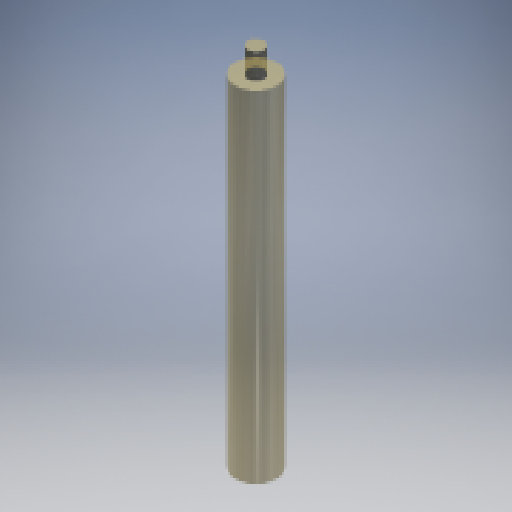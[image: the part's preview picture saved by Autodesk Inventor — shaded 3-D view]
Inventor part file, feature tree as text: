
AUTODESK INVENTOR PART (.ipt)
format: ipt  version: 2024.3 (Build 283343000, 343)  size: 295,424 bytes
history: native  units: mm
features: extrude x2, sketch x2, thread x1, hole x1
ambient origin geometry x8: Origin, YZ Plane, XZ Plane, XY Plane, X Axis, Y Axis, Z Axis, Center Point
bodies: Volumenkörper1 (feature_tree)
feature tree (6):
  extrude  "Extrusion1"  Depth=82.0mm TaperAngle=0.0deg
  extrude  "Extrusion2"  Depth=6.0mm TaperAngle=0.0deg
  thread  "Gewinde1"  [1 undecoded]
  hole  "Bohrung1"  [1 undecoded]
  sketch  "Skizze2"  dims[d0=10.0mm d1=82.0mm d2=0.0mm]
  sketch  "Skizze3"  dims[d3=4.0mm d4=6.0mm d5=0.0mm d6=6.0mm d7=0.0mm d8=4.134mm d9=10.0mm d10=4.0mm d11=2.0mm d12=90.0deg d13=14.2mm d14=20.594885mm]
note: 2 required parameter values undecoded (feature->parameter linkage not recoverable at this tier; creation-order binding heuristic only, values carry confidence <= 0.55)
